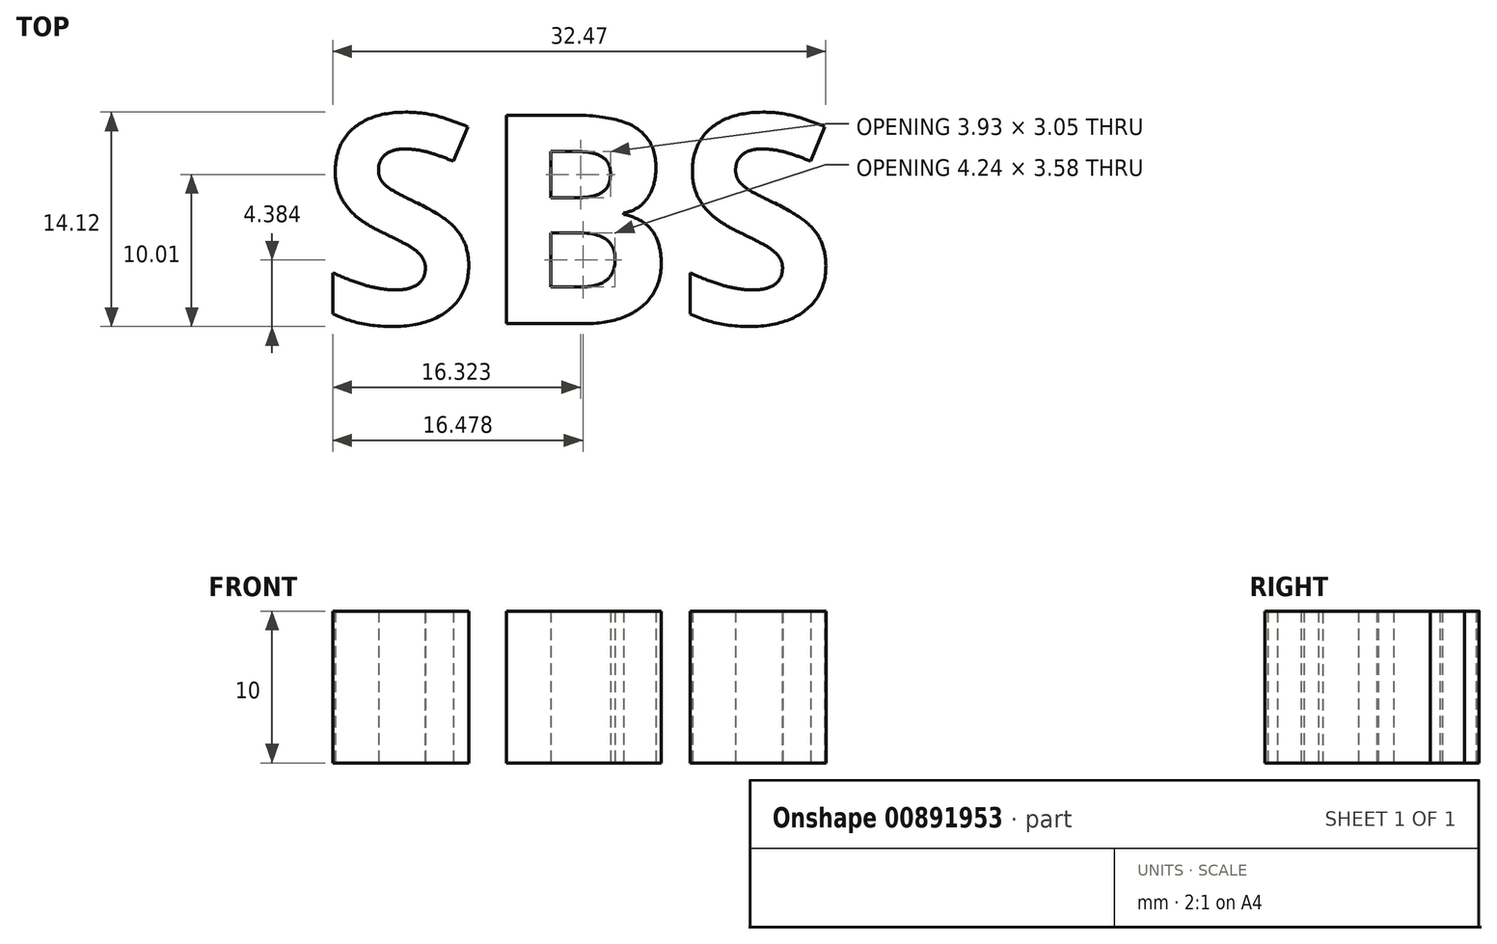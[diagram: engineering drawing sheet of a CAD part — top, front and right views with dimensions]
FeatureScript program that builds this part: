
annotation { "Feature Type Name" : "Feature", "Feature Type Description" : "" }
export const myFeature = defineFeature(function(context is Context, id is Id, definition is map)
    precondition{}
    {
        {
            var Q0;
            Q0=qCreatedBy(makeId("Front.planeOp"),FACE);
            var sketch = newSketch(context, id + "F0", { "sketchPlane" : qUnion([Q0])});
            skLineSegment(sketch, "E0", {"start": v(-38.5, 0) * mm, "end": v(-38.5, 12.5) * mm});
            skLineSegment(sketch, "E1", {"start": v(-38.5, 12.5) * mm, "end": v(-25, 12.5) * mm});
            skLineSegment(sketch, "E2", {"start": v(-25, 12.5) * mm, "end": v(-25, 15.3) * mm});
            skLineSegment(sketch, "E3", {"start": v(-25, 15.3) * mm, "end": v(0, 15.3) * mm});
            skLineSegment(sketch, "E4", {"start": v(0, 22.8) * mm, "end": v(-46, 22.8) * mm});
            skLineSegment(sketch, "E5", {"start": v(-46, 22.8) * mm, "end": v(-46, 0) * mm});
            skLineSegment(sketch, "E6", {"start": v(-46, 0) * mm, "end": v(-38.5, 0) * mm});
            skLineSegment(sketch, "E7", {"start": v(0, 22.8) * mm, "end": v(0, 15.3) * mm});
            skSolve(sketch);
        }
        {
            var Q0;
            Q0=sQuery(id+"F0.wireOp",EDGE,"E3");
            var Q1;
            Q1=sQuery(id+"F0.wireOp",EDGE,"E4");
            var Q2;
            Q2=sQuery(id+"F0.wireOp",EDGE,"E0");
            var Q3;
            Q3=sQuery(id+"F0.wireOp",EDGE,"E1");
            var Q4;
            Q4=sQuery(id+"F0.wireOp",EDGE,"E5");
            var Q5;
            Q5=sQuery(id+"F0.wireOp",EDGE,"E6");
            var Q6;
            Q6=sQuery(id+"F0.wireOp",EDGE,"E2");
            var Q7;
            Q7=sQuery(id+"F0.wireOp",EDGE,"E7");
            revolve(context, id + "F1", {"bodyType" : ToolBodyType.SURFACE, "surfaceOperationType" : NewSurfaceOperationType.NEW, "surfaceEntities" : qUnion([Q0, Q1, Q2, Q3, Q4, Q5, Q6]), "axis" : qUnion([Q7]), "revolveType" : RevolveType.FULL});
        }
        {
            var Q0;
            Q0=makeQuery(id+"F1.opRevolve","SWEPT_FACE",FACE,{"disambiguationData":[OSD([sQuery(id+"F0.wireOp",EDGE,"E3")])]});
            var sketch = newSketch(context, id + "F2", { "sketchPlane" : qUnion([Q0])});
            skText(sketch, "E8", { "text": "SBS", "fontName": "OpenSans-Bold.ttf"});
            const initialGuessF2  = {"E8": [-0.01726, -0.00692, 1, 0, 0.01385]};
            skSetInitialGuess(sketch, initialGuessF2);
            skSolve(sketch);
        }
        {
            var Q0;
            Q0 = qSketchRegion(id + "F2", true);
            extrude(context, id + "F3", {"entities" : qUnion([Q0]), "depth" : 10 * mm, "offsetDistance" : 25 * mm});
        }
    });
